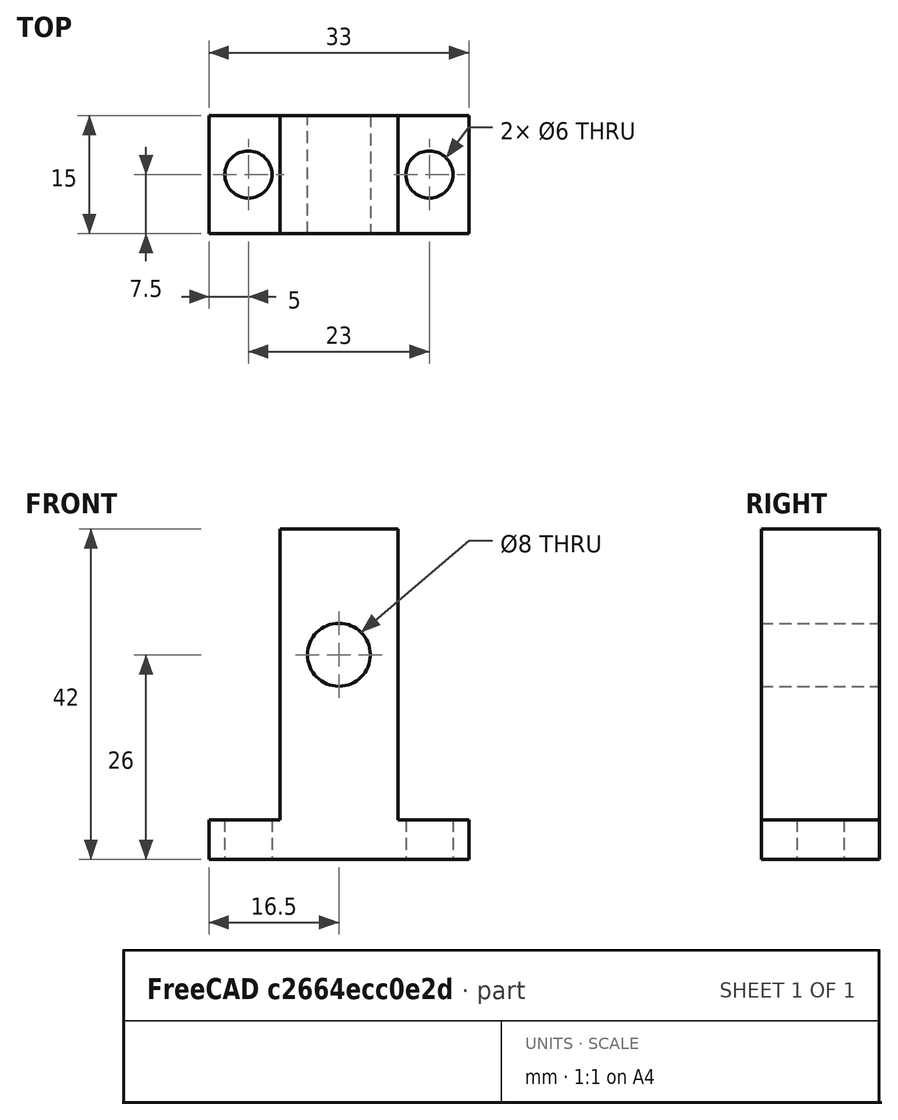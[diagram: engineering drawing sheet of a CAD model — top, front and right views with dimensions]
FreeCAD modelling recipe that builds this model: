
FCSTD DOCUMENT  (FreeCAD 0.18R4 (GitTag))
Label: soporte_guia
License: All rights reserved
LicenseURL: http://en.wikipedia.org/wiki/All_rights_reserved
objects: Sketcher::SketchObject×2, PartDesign::Body×1, PartDesign::Pad×1, PartDesign::Hole×1
note: 7 computed .brp shape members not serialized (recipe doc carries the construction recipe); baked Part::Feature solids carry a one-line shape summary decoded from their .brp

FEATURE [PartDesign::Body] Body
  Group = -> [Sketch,Pad,Sketch001,Hole]
  Origin = -> Origin
  Tip = -> Hole
FEATURE [Sketcher::SketchObject] Sketch
  MapMode = 2
  Placement = pos=(1.2e-15,-10,15) rot=(0,0,1;3.14159rad)
  Support = -> [Sketch001]
  sketch-geometry (9):
    g0: LineSegment StartX=0 StartY=0 StartZ=0 EndX=33 EndY=0 EndZ=0
    g1: LineSegment StartX=33 StartY=0 StartZ=0 EndX=33 EndY=5 EndZ=0
    g2: LineSegment StartX=24 StartY=42 StartZ=0 EndX=9 EndY=42 EndZ=0
    g3: LineSegment StartX=0 StartY=5 StartZ=0 EndX=0 EndY=0 EndZ=0
    g4: Circle CenterX=16.5 CenterY=26 CenterZ=0 NormalX=0 NormalY=0 NormalZ=1 AngleXU=0 Radius=4
    g5: LineSegment StartX=9 StartY=42 StartZ=0 EndX=9 EndY=5 EndZ=0
    g6: LineSegment StartX=9 StartY=5 StartZ=0 EndX=0 EndY=5 EndZ=0
    g7: LineSegment StartX=33 StartY=5 StartZ=0 EndX=24 EndY=5 EndZ=0
    g8: LineSegment StartX=24 StartY=5 StartZ=0 EndX=24 EndY=42 EndZ=0
  constraints (26):
    c: Coincident(g0,g1)
    c: Coincident(g3,g0)
    c: Horizontal(g0)
    c: Horizontal(g2)
    c: Vertical(g1)
    c: Vertical(g3)
    c: DistanceX(g0,g0) = 33
    c: Coincident(g0,g-1)
    c: Radius(g4) = 4
    c: Distance(g4,g3) = 16.5
    c: Distance(g4,g0) = 26
    c: Coincident(g5,g6)
    c: Horizontal(g6)
    c: Vertical(g5)
    c: Coincident(g7,g8)
    c: Horizontal(g7)
    c: Vertical(g8)
    c: DistanceY(g5,g5) = 37
    c: DistanceY(g8,g8) = 37
    c: DistanceX(g6,g6) = 9
    c: DistanceX(g7,g7) = 9
    c: DistanceY(g3,g3) = 5
    c: Coincident(g1,g7)
    c: Coincident(g2,g8)
    c: Coincident(g2,g5)
    c: Coincident(g3,g6)
FEATURE [PartDesign::Pad] Pad
  Length = 15
  Length2 = 100
  Placement = pos=(1.2e-15,-10,15) rot=(0,0,1;3.14159rad)
  Profile = -> Sketch
  Type = 0
FEATURE [Sketcher::SketchObject] Sketch001
  MapMode = 5
  Placement = pos=(1.2e-15,-10,15) rot=(0,0,1;3.14159rad)
  Support = -> [Pad]
  sketch-geometry (2):
    g0: Circle CenterX=-28 CenterY=7.5 CenterZ=0 NormalX=0 NormalY=0 NormalZ=1 AngleXU=0 Radius=2.5
    g1: Circle CenterX=-5 CenterY=7.5 CenterZ=0 NormalX=0 NormalY=0 NormalZ=1 AngleXU=0 Radius=2.5
  constraints (6):
    c: Radius(g1) = 2.5
    c: Radius(g0) = 2.5
    c: DistanceX(g1,g-1) = 5
    c: DistanceX(g0,g-1) = 28
    c: DistanceY(g-1,g1) = 7.5
    c: DistanceY(g-1,g0) = 7.5
FEATURE [PartDesign::Hole] Hole
  BaseFeature = -> Pad
  Depth = 25
  DepthType = 0
  Diameter = 6
  DrillPoint = 1
  DrillPointAngle = 118
  HoleCutCountersinkAngle = 90
  HoleCutDepth = 0
  HoleCutDiameter = 0
  HoleCutType = 0
  ModelActualThread = false
  Placement = pos=(1.2e-15,-10,15) rot=(0,0,1;3.14159rad)
  Profile = -> Sketch001
  Tapered = false
  TaperedAngle = 90
  ThreadAngle = 0
  ThreadClass = 0
  ThreadCutOffInner = 0
  ThreadCutOffOuter = 0
  ThreadDirection = 0
  ThreadFit = 0
  ThreadPitch = 0
  ThreadSize = 0
  ThreadType = 0
  Threaded = false
